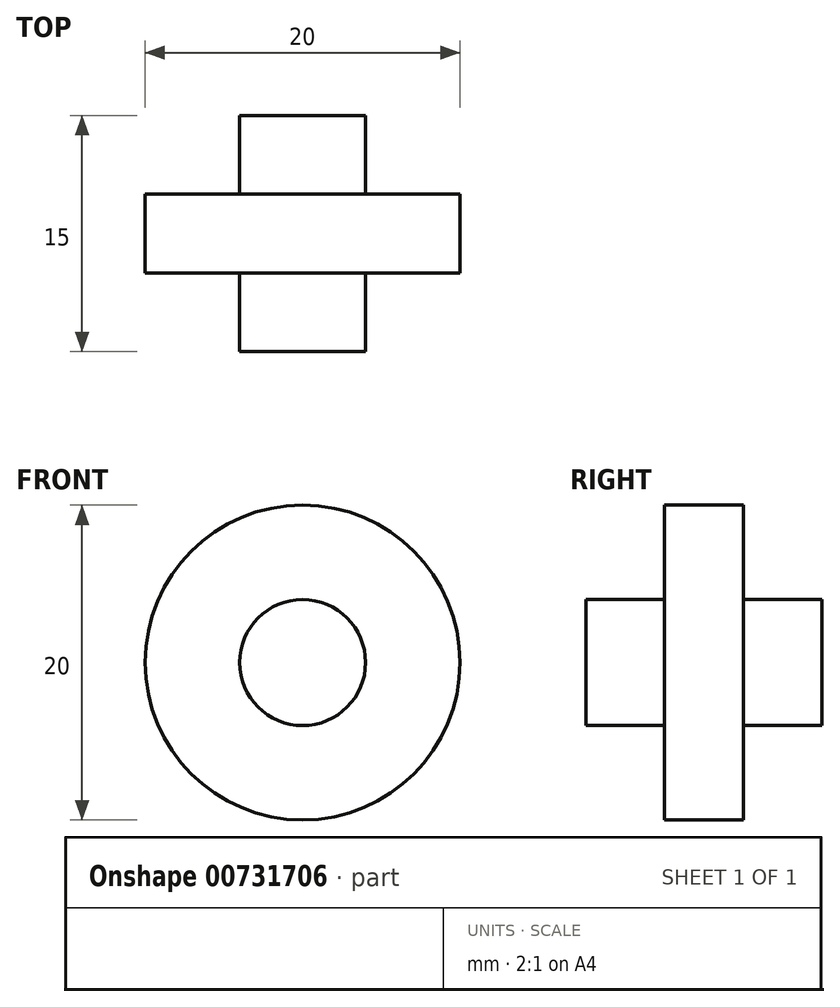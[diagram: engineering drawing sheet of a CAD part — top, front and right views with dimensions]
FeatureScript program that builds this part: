
annotation { "Feature Type Name" : "Feature", "Feature Type Description" : "" }
export const myFeature = defineFeature(function(context is Context, id is Id, definition is map)
    precondition{}
    {
        {
            var Q0;
            Q0=qCreatedBy(makeId("Front.planeOp"),FACE);
            var sketch = newSketch(context, id + "F0", { "sketchPlane" : qUnion([Q0])});
            skCircle(sketch, "E0", {"center": v(-46.32, 31.3) * mm, "radius": 4 * mm});
            skCircle(sketch, "E1", {"center": v(-46.32, 31.3) * mm, "radius": 10 * mm});
            skSolve(sketch);
        }
        {
            var Q0;
            Q0=makeQuery(id+"F0.imprint","IMPRINT",FACE,{"disambiguationData":[TD([[makeQuery(id+"F0.imprint","IMPRINT",EDGE,{"derivedFrom":sQuery(id+"F0.wireOp",EDGE,"E0")}),-1.0]])]});
            extrude(context, id + "F1", {"entities" : qUnion([Q0]), "depth" : 5 * mm, "offsetDistance" : 25 * mm});
        }
        {
            var Q0;
            Q0=makeQuery(id+"F0.imprint","IMPRINT",FACE,{"disambiguationData":[TD([[makeQuery(id+"F0.imprint","IMPRINT",EDGE,{"derivedFrom":sQuery(id+"F0.wireOp",EDGE,"E0")}),1.0]])]});
            extrude(context, id + "F2", {"entities" : qUnion([Q0]), "operationType" : NewBodyOperationType.ADD, "depth" : 10 * mm, "offsetDistance" : 25 * mm, "hasSecondDirection" : true, "secondDirectionOppositeDirection" : true, "secondDirectionDepth" : 5 * mm});
        }
    });
